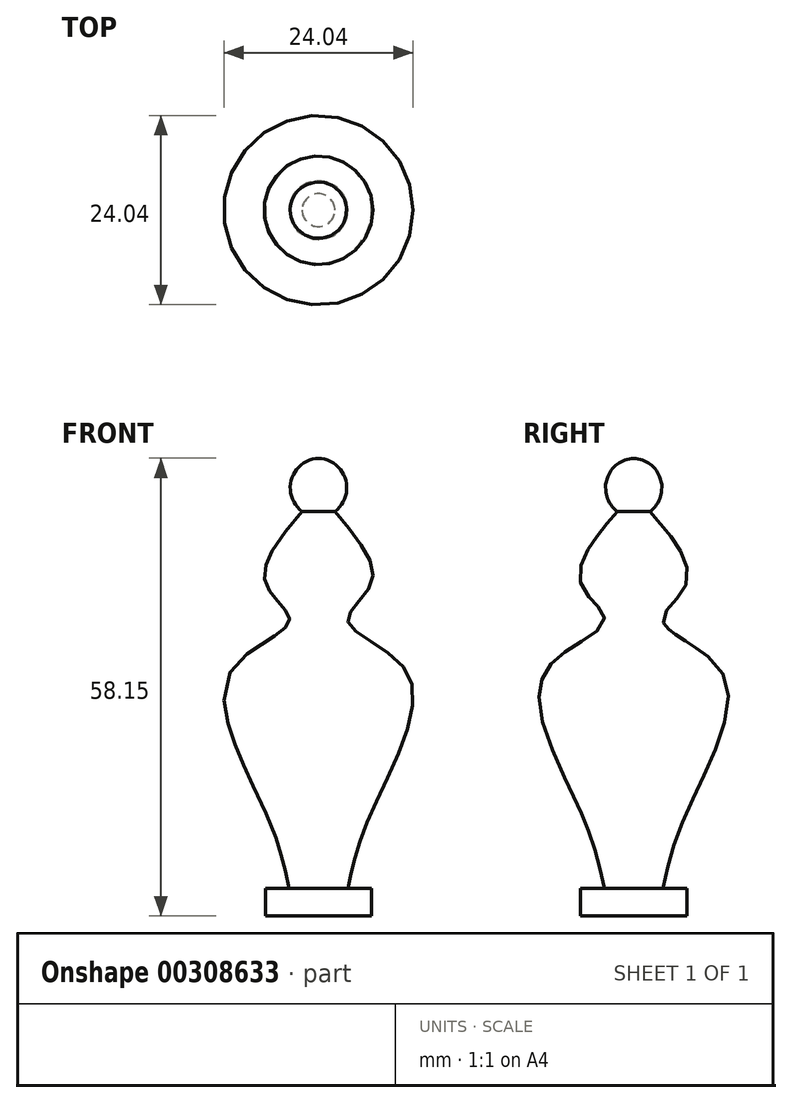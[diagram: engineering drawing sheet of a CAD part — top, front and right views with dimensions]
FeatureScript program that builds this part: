
annotation { "Feature Type Name" : "Feature", "Feature Type Description" : "" }
export const myFeature = defineFeature(function(context is Context, id is Id, definition is map)
    precondition{}
    {
        {
            var Q0;
            Q0=qCreatedBy(makeId("Front.planeOp"),FACE);
            var sketch = newSketch(context, id + "F0", { "sketchPlane" : qUnion([Q0])});
            skLineSegment(sketch, "E0", {"start": v(0, 27.45) * mm, "end": v(0, -30.7) * mm});
            skLineSegment(sketch, "E1", {"start": v(0, -30.7) * mm, "end": v(-6.75, -30.7) * mm});
            skLineSegment(sketch, "E2", {"start": v(-6.75, -30.7) * mm, "end": v(-6.75, -27.21) * mm});
            skLineSegment(sketch, "E3", {"start": v(-6.75, -27.21) * mm, "end": v(-3.72, -27.21) * mm});
            skFitSpline(sketch, "E4", {"points": [v(-3.72, -27.21) * mm, v(-6.75, -17.44) * mm, v(-11.4, 0) * mm, v(-3.72, 6.75) * mm, v(-6.75, 11.63) * mm, v(-2.1, 20.7) * mm], "startDerivative": vector(-9.23, 43.34) * mm, "endDerivative": vector(41.93, 49.51) * mm});
            skArc(sketch, "E5", {"start": v(0, 27.45) * mm, "mid": v(-3.42, 24.81) * mm, "end": v(-2.1, 20.7) * mm});
            skSolve(sketch);
        }
        {
            var Q0;
            Q0 = qSketchRegion(id + "F0", true);
            var Q1;
            Q1=sQuery(id+"F0.wireOp",EDGE,"E0");
            revolve(context, id + "F1", {"entities" : qUnion([Q0]), "axis" : qUnion([Q1]), "revolveType" : RevolveType.FULL});
        }
    });
